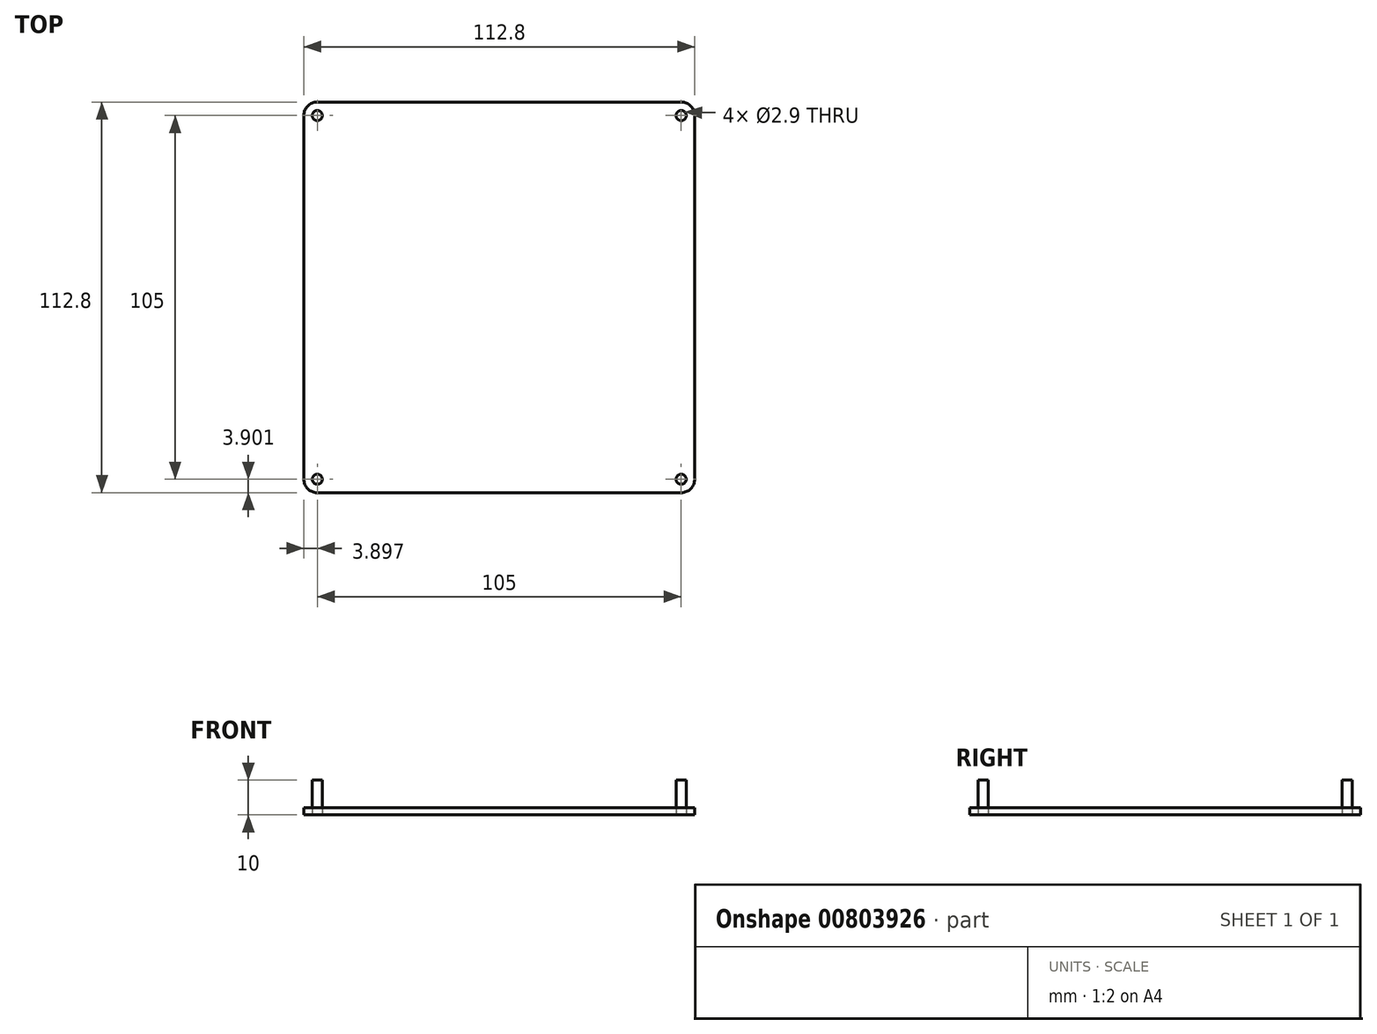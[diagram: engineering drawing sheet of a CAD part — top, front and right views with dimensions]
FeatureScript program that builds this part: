
annotation { "Feature Type Name" : "Feature", "Feature Type Description" : "" }
export const myFeature = defineFeature(function(context is Context, id is Id, definition is map)
    precondition{}
    {
        {
            var Q0;
            Q0=qCreatedBy(makeId("Top.planeOp"),FACE);
            var sketch = newSketch(context, id + "F0", { "sketchPlane" : qUnion([Q0])});
            skArc(sketch, "E0.0", {"start": v(-53.2, 59.2) * mm, "mid": v(-56.03, 58.02) * mm, "end": v(-57.2, 55.2) * mm, "construction": true});
            skLineSegment(sketch, "E0.2", {"start": v(-53.2, 59.2) * mm, "end": v(51.8, 59.2) * mm, "construction": true});
            skArc(sketch, "E0.4", {"start": v(55.8, 55.2) * mm, "mid": v(54.63, 58.02) * mm, "end": v(51.8, 59.2) * mm, "construction": true});
            skLineSegment(sketch, "E0.5", {"start": v(55.8, 55.2) * mm, "end": v(55.8, -49.8) * mm, "construction": true});
            skArc(sketch, "E0.6", {"start": v(51.8, -53.8) * mm, "mid": v(54.63, -52.64) * mm, "end": v(55.8, -49.8) * mm, "construction": true});
            skLineSegment(sketch, "E0.7", {"start": v(51.8, -53.8) * mm, "end": v(-53.2, -53.8) * mm, "construction": true});
            skArc(sketch, "E0.8", {"start": v(-57.2, -49.8) * mm, "mid": v(-56.03, -52.64) * mm, "end": v(-53.2, -53.8) * mm, "construction": true});
            skLineSegment(sketch, "E1", {"start": v(-57.2, 55.2) * mm, "end": v(-57.2, -49.8) * mm, "construction": true});
            skSolve(sketch);
        }
        {
            var Q0;
            Q0=qCreatedBy(makeId("Top.planeOp"),FACE);
            var sketch = newSketch(context, id + "F1", { "sketchPlane" : qUnion([Q0])});
            skArc(sketch, "E2.0", {"start": v(-53.2, 59.2) * mm, "mid": v(-56.03, 58.02) * mm, "end": v(-57.2, 55.2) * mm, "construction": true});
            skLineSegment(sketch, "E2.1", {"start": v(-53.2, 59.2) * mm, "end": v(51.8, 59.2) * mm, "construction": true});
            skLineSegment(sketch, "E2.2", {"start": v(55.8, 55.2) * mm, "end": v(55.8, -49.8) * mm, "construction": true});
            skLineSegment(sketch, "E2.3", {"start": v(51.8, -53.8) * mm, "end": v(-53.2, -53.8) * mm, "construction": true});
            skLineSegment(sketch, "E2.4", {"start": v(-57.2, 55.2) * mm, "end": v(-57.2, -49.8) * mm, "construction": true});
            skArc(sketch, "E2.5", {"start": v(55.8, 55.2) * mm, "mid": v(54.63, 58.02) * mm, "end": v(51.8, 59.2) * mm, "construction": true});
            skArc(sketch, "E2.6", {"start": v(51.8, -53.8) * mm, "mid": v(54.63, -52.64) * mm, "end": v(55.8, -49.8) * mm, "construction": true});
            skArc(sketch, "E2.7", {"start": v(-57.2, -49.8) * mm, "mid": v(-56.03, -52.64) * mm, "end": v(-53.2, -53.8) * mm, "construction": true});
            skCircle(sketch, "E3", {"center": v(-53.2, 55.2) * mm, "radius": 1.45 * mm});
            skCircle(sketch, "E4", {"center": v(51.8, 55.2) * mm, "radius": 1.45 * mm});
            skCircle(sketch, "E5", {"center": v(51.8, -49.8) * mm, "radius": 1.45 * mm});
            skCircle(sketch, "E6", {"center": v(-53.2, -49.8) * mm, "radius": 1.45 * mm});
            skLineSegment(sketch, "E7", {"start": v(-57.1, 55.2) * mm, "end": v(-57.1, -49.8) * mm});
            skLineSegment(sketch, "E8", {"start": v(55.7, 55.2) * mm, "end": v(55.7, -49.8) * mm});
            skLineSegment(sketch, "E9", {"start": v(51.8, -53.7) * mm, "end": v(-53.2, -53.7) * mm});
            skLineSegment(sketch, "E10", {"start": v(-53.2, 59.1) * mm, "end": v(51.8, 59.1) * mm});
            skArc(sketch, "E11", {"start": v(-53.2, 59.1) * mm, "mid": v(-55.96, 57.95) * mm, "end": v(-57.1, 55.2) * mm});
            skArc(sketch, "E12", {"start": v(55.7, 55.2) * mm, "mid": v(54.56, 57.95) * mm, "end": v(51.8, 59.1) * mm});
            skArc(sketch, "E13", {"start": v(51.8, -53.7) * mm, "mid": v(54.56, -52.57) * mm, "end": v(55.7, -49.8) * mm});
            skArc(sketch, "E14", {"start": v(-57.1, -49.8) * mm, "mid": v(-55.96, -52.57) * mm, "end": v(-53.2, -53.7) * mm});
            skSolve(sketch);
        }
        {
            var Q0;
            Q0=makeQuery(id+"F1.imprint","IMPRINT",FACE,{"disambiguationData":[TD([[makeQuery(id+"F1.imprint","IMPRINT",EDGE,{"derivedFrom":sQuery(id+"F1.wireOp",EDGE,"E3")}),-1.0]])]});
            extrude(context, id + "F2", {"entities" : qUnion([Q0]), "depth" : 2 * mm, "offsetDistance" : 25 * mm});
        }
        {
            var Q0;
            Q0=makeQuery(id+"F1.imprint","IMPRINT",FACE,{"disambiguationData":[TD([[makeQuery(id+"F1.imprint","IMPRINT",EDGE,{"derivedFrom":sQuery(id+"F1.wireOp",EDGE,"E3")}),1.0]])]});
            var Q1;
            Q1=makeQuery(id+"F1.imprint","IMPRINT",FACE,{"disambiguationData":[TD([[makeQuery(id+"F1.imprint","IMPRINT",EDGE,{"derivedFrom":sQuery(id+"F1.wireOp",EDGE,"E4")}),1.0]])]});
            var Q2;
            Q2=makeQuery(id+"F1.imprint","IMPRINT",FACE,{"disambiguationData":[TD([[makeQuery(id+"F1.imprint","IMPRINT",EDGE,{"derivedFrom":sQuery(id+"F1.wireOp",EDGE,"E6")}),1.0]])]});
            var Q3;
            Q3=makeQuery(id+"F1.imprint","IMPRINT",FACE,{"disambiguationData":[TD([[makeQuery(id+"F1.imprint","IMPRINT",EDGE,{"derivedFrom":sQuery(id+"F1.wireOp",EDGE,"E5")}),1.0]])]});
            extrude(context, id + "F3", {"entities" : qUnion([Q0, Q1, Q2, Q3]), "depth" : 10 * mm, "offsetDistance" : 25 * mm});
        }
    });
